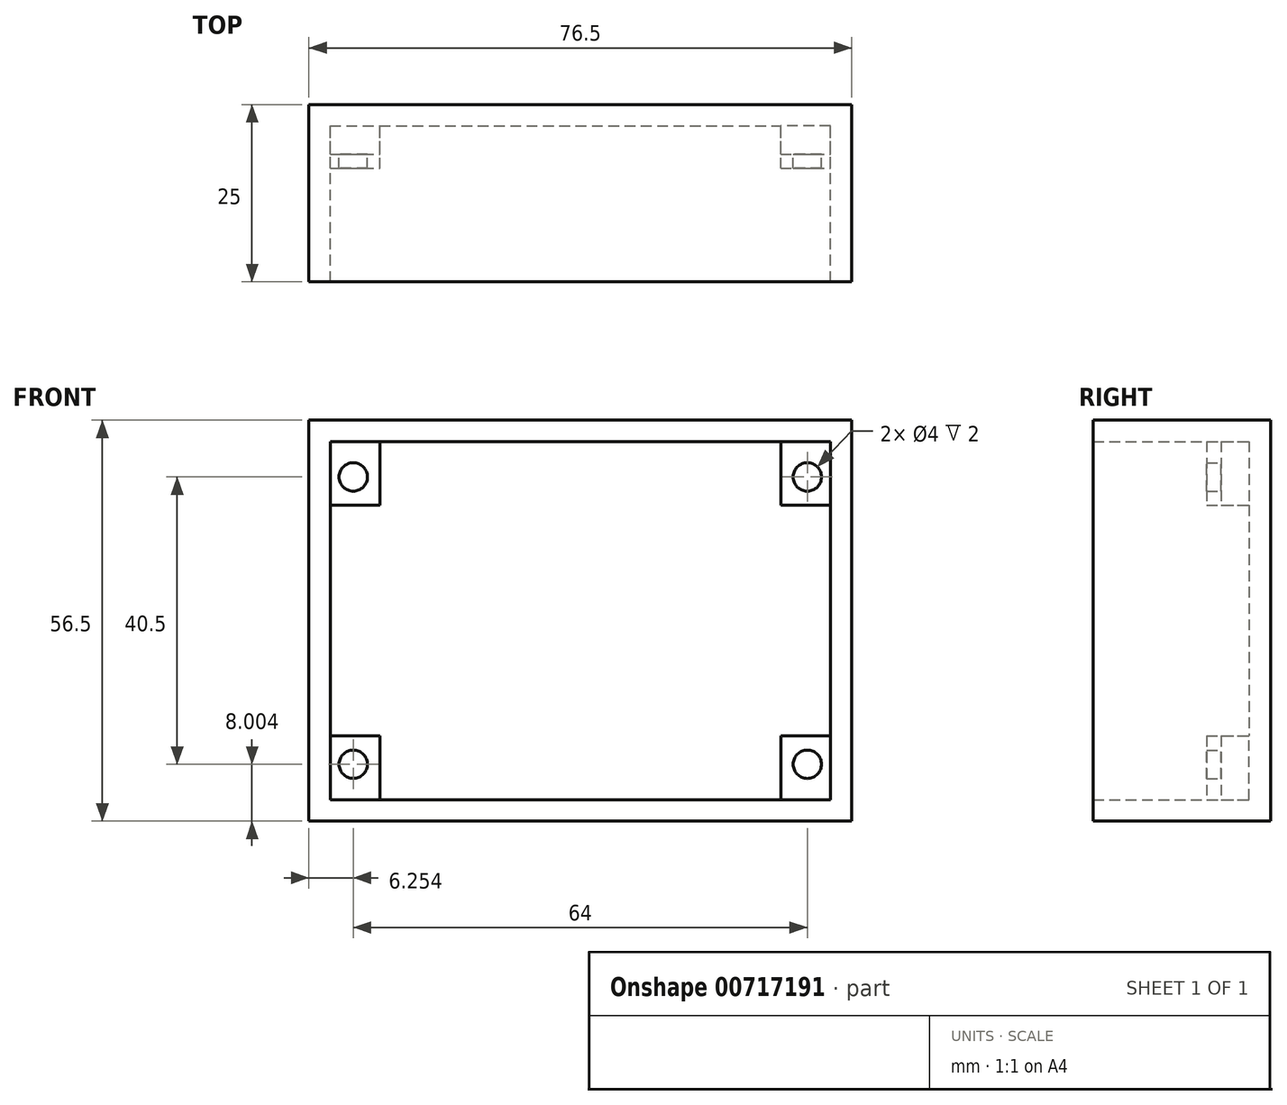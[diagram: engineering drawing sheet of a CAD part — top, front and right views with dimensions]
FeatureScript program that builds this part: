
annotation { "Feature Type Name" : "Feature", "Feature Type Description" : "" }
export const myFeature = defineFeature(function(context is Context, id is Id, definition is map)
    precondition{}
    {
        {
            var Q0;
            Q0=qCreatedBy(makeId("Front.planeOp"),FACE);
            var sketch = newSketch(context, id + "F0", { "sketchPlane" : qUnion([Q0])});
            skLineSegment(sketch, "E0.bottom", {"start": v(-25.92, 32.71) * mm, "end": v(50.58, 32.71) * mm});
            skLineSegment(sketch, "E0.top", {"start": v(-25.92, -23.79) * mm, "end": v(50.58, -23.79) * mm});
            skLineSegment(sketch, "E0.left", {"start": v(-25.92, 32.71) * mm, "end": v(-25.92, -23.79) * mm});
            skLineSegment(sketch, "E0.right", {"start": v(50.58, 32.71) * mm, "end": v(50.58, -23.79) * mm});
            skLineSegment(sketch, "E1.0", {"start": v(-22.92, 29.71) * mm, "end": v(47.58, 29.71) * mm});
            skLineSegment(sketch, "E1.1", {"start": v(-22.92, 29.71) * mm, "end": v(-22.92, -20.79) * mm});
            skLineSegment(sketch, "E1.2", {"start": v(-22.92, -20.79) * mm, "end": v(47.58, -20.79) * mm});
            skLineSegment(sketch, "E1.3", {"start": v(47.58, 29.71) * mm, "end": v(47.58, -20.79) * mm});
            skCircle(sketch, "E2", {"center": v(-19.67, 24.71) * mm, "radius": 2 * mm});
            skPoint(sketch, "E3", {"position": v(12.33, 29.71) * mm});
            skPoint(sketch, "E4", {"position": v(12.33, -20.79) * mm});
            skLineSegment(sketch, "E5", {"start": v(12.33, 29.71) * mm, "end": v(12.33, -20.79) * mm});
            skPoint(sketch, "E6", {"position": v(-22.92, 4.46) * mm});
            skPoint(sketch, "E7", {"position": v(47.58, 4.46) * mm});
            skLineSegment(sketch, "E8", {"start": v(-22.92, 4.46) * mm, "end": v(47.58, 4.46) * mm});
            skCircle(sketch, "E9.MirrorC", {"center": v(44.33, 24.71) * mm, "radius": 2 * mm});
            skCircle(sketch, "E10.MirrorC", {"center": v(-19.67, -15.79) * mm, "radius": 2 * mm});
            skCircle(sketch, "E11.MirrorC", {"center": v(44.33, -15.79) * mm, "radius": 2 * mm});
            skPoint(sketch, "E12", {"position": v(-17.67, 24.7) * mm});
            skLineSegment(sketch, "E13.bottom", {"start": v(-22.92, 29.71) * mm, "end": v(-15.92, 29.71) * mm});
            skLineSegment(sketch, "E13.top", {"start": v(-22.92, 20.71) * mm, "end": v(-15.92, 20.71) * mm});
            skLineSegment(sketch, "E13.left", {"start": v(-22.92, 29.71) * mm, "end": v(-22.92, 20.71) * mm});
            skLineSegment(sketch, "E13.right", {"start": v(-15.92, 29.71) * mm, "end": v(-15.92, 20.71) * mm});
            skLineSegment(sketch, "E14.MirrorCS", {"start": v(47.58, 20.71) * mm, "end": v(40.58, 20.71) * mm});
            skLineSegment(sketch, "E15.MirrorCS", {"start": v(40.58, 29.71) * mm, "end": v(40.58, 20.71) * mm});
            skLineSegment(sketch, "E16.MirrorCS", {"start": v(47.58, 4.46) * mm, "end": v(-22.92, 4.46) * mm});
            skLineSegment(sketch, "E17.MirrorCS", {"start": v(-22.92, -11.79) * mm, "end": v(-15.92, -11.79) * mm});
            skLineSegment(sketch, "E18.MirrorCS", {"start": v(-15.92, -20.79) * mm, "end": v(-15.92, -11.79) * mm});
            skLineSegment(sketch, "E19.MirrorCS", {"start": v(47.58, -11.79) * mm, "end": v(40.58, -11.79) * mm});
            skLineSegment(sketch, "E20.MirrorCS", {"start": v(40.58, -20.79) * mm, "end": v(40.58, -11.79) * mm});
            skSolve(sketch);
        }
        {
            var Q0;
            Q0=makeQuery(id+"F0.imprint","IMPRINT",FACE,{"disambiguationData":[TD([[makeQuery(id+"F0.imprint","IMPRINT",EDGE,{"derivedFrom":sQuery(id+"F0.wireOp",EDGE,"E0.bottom")}),-1.0]])]});
            extrude(context, id + "F1", {"entities" : qUnion([Q0]), "depth" : 25 * mm, "offsetDistance" : 25 * mm});
        }
        {
            var Q0;
            {var subQ0=sQuery(id+"F0.wireOp",EDGE,"E13.top");Q0=makeQuery(id+"F0.imprint","IMPRINT",FACE,{"disambiguationData":[TD([[makeQuery(id+"F0.imprint","IMPRINT",EDGE,{"derivedFrom":subQ0}),-1.0]])]});}
            var Q1;
            {var subQ0=sQuery(id+"F0.wireOp",EDGE,"E14.MirrorCS");Q1=makeQuery(id+"F0.imprint","IMPRINT",FACE,{"disambiguationData":[TD([[makeQuery(id+"F0.imprint","IMPRINT",EDGE,{"derivedFrom":subQ0}),1.0]])]});}
            var Q2;
            {var subQ7=sQuery(id+"F0.wireOp",EDGE,"E19.MirrorCS");Q2=makeQuery(id+"F0.imprint","IMPRINT",FACE,{"disambiguationData":[TD([[makeQuery(id+"F0.imprint","IMPRINT",EDGE,{"derivedFrom":subQ7}),-1.0]])]});}
            var Q3;
            {var subQ5=sQuery(id+"F0.wireOp",EDGE,"E17.MirrorCS");Q3=makeQuery(id+"F0.imprint","IMPRINT",FACE,{"disambiguationData":[TD([[makeQuery(id+"F0.imprint","IMPRINT",EDGE,{"derivedFrom":subQ5}),1.0]])]});}
            extrude(context, id + "F2", {"entities" : qUnion([Q0, Q1, Q2, Q3]), "operationType" : NewBodyOperationType.ADD, "depth" : 3 * mm, "offsetDistance" : 25 * mm});
        }
        {
            var Q0;
            Q0=makeQuery(id+"F0.imprint","IMPRINT",FACE,{"disambiguationData":[TD([[makeQuery(id+"F0.imprint","IMPRINT",EDGE,{"derivedFrom":sQuery(id+"F0.wireOp",EDGE,"E2")}),-1.0]])]});
            var Q1;
            Q1=makeQuery(id+"F0.imprint","IMPRINT",FACE,{"disambiguationData":[TD([[makeQuery(id+"F0.imprint","IMPRINT",EDGE,{"derivedFrom":sQuery(id+"F0.wireOp",EDGE,"E9.MirrorC")}),1.0]])]});
            var Q2;
            Q2=makeQuery(id+"F0.imprint","IMPRINT",FACE,{"disambiguationData":[TD([[makeQuery(id+"F0.imprint","IMPRINT",EDGE,{"derivedFrom":sQuery(id+"F0.wireOp",EDGE,"E11.MirrorC")}),-1.0]])]});
            var Q3;
            Q3=makeQuery(id+"F0.imprint","IMPRINT",FACE,{"disambiguationData":[TD([[makeQuery(id+"F0.imprint","IMPRINT",EDGE,{"derivedFrom":sQuery(id+"F0.wireOp",EDGE,"E10.MirrorC")}),1.0]])]});
            extrude(context, id + "F3", {"entities" : qUnion([Q0, Q1, Q2, Q3]), "operationType" : NewBodyOperationType.ADD, "depth" : 7 * mm, "offsetDistance" : 25 * mm});
        }
        {
            var Q0;
            Q0=makeQuery(id+"F0.imprint","IMPRINT",FACE,{"disambiguationData":[TD([[makeQuery(id+"F0.imprint","IMPRINT",EDGE,{"derivedFrom":sQuery(id+"F0.wireOp",EDGE,"E2")}),1.0]])]});
            var Q1;
            Q1=makeQuery(id+"F0.imprint","IMPRINT",FACE,{"disambiguationData":[TD([[makeQuery(id+"F0.imprint","IMPRINT",EDGE,{"derivedFrom":sQuery(id+"F0.wireOp",EDGE,"E11.MirrorC")}),1.0]])]});
            extrude(context, id + "F4", {"entities" : qUnion([Q0, Q1]), "operationType" : NewBodyOperationType.ADD, "depth" : 9 * mm, "offsetDistance" : 25 * mm});
        }
        {
            var Q0;
            Q0=makeQuery(id+"F0.imprint","IMPRINT",FACE,{"disambiguationData":[TD([[makeQuery(id+"F0.imprint","IMPRINT",EDGE,{"derivedFrom":sQuery(id+"F0.wireOp",EDGE,"E9.MirrorC")}),-1.0]])]});
            extrude(context, id + "F5", {"entities" : qUnion([Q0]), "operationType" : NewBodyOperationType.ADD, "depth" : 9 * mm, "offsetDistance" : 25 * mm});
        }
        {
            var Q0;
            Q0=makeQuery(id+"F0.imprint","IMPRINT",FACE,{"disambiguationData":[TD([[makeQuery(id+"F0.imprint","IMPRINT",EDGE,{"derivedFrom":sQuery(id+"F0.wireOp",EDGE,"E10.MirrorC")}),-1.0]])]});
            extrude(context, id + "F6", {"entities" : qUnion([Q0]), "operationType" : NewBodyOperationType.ADD, "depth" : 9 * mm, "offsetDistance" : 25 * mm});
        }
    });
